# Revit family: Maxlogic  Module  E- S  Adressable Intelligent
name_source: partatom
category: Fire Alarm Devices
units: mm (PartAtom-declared; Revit-internal decimal feet)

## family parameters
Cut with Voids When Loaded = No
Host = Face
Maintain Annotation Orientation = Yes
OmniClass Number = 23.85.30.21
OmniClass Title = Environmental Detection/Registration
Part Type = Normal
Room Calculation Point = No
Round Connector Dimension = Use Diameter
Shared = No

## types (9) — shared parameters
Adresse ligne 1 = Şerifali Mahallesi Kutup Sokak No:27/1-2-4 Ümraniye TR-34775 İSTANBUL
Couleur = Blanc
Deuxime Matèriel = Plastique
Durée de la garantie Travail = 2
Durée de la garantie réservé = 2
Hauteur Nominale = 100 mm
Largeur Nominale = 52 mm
Longeur Nominale = 100 mm
Manuel d'installation = https://mavilielektronik.com
Manufacturer = Mavili Elektronik Ticaret A.Ş.
Matériel Principe = Plastique Blanche PC/ABS
Model = MaxLogic
Numèro de Fax = (+)90 216 466 45 10
Poids = 135 gr
Surface de Montage = Montage à Mur
Tempèrature de Fonctionnement = (-10°C) - (+55°C)
URL = https://www.mavili.com.tr
Unité de durée de garantie = Ans
Voltage de fonctionnement (default) = 26 V/DC
voltage fonction d'opération = 18-33V/DC
zero-valued in all types: Cost, Default Elevation

## per-type parameters (varying)
| type | Charger adresse d'appareil | Code de  Performance | Code de Produit | Description | Numéro de pose des travaux publics |
| Maxlogic Relais Contrôle de Module Adressable, 1 Sortie | Appareil d'adressage à Main | EN 54-18 | ML-1361 | Adresli röle kontrol modülü, 1 çıkış | 833-570 |
| Maxlogic Relais Contrôle de Module Adressable, Isolateur de Court-Circuit | Appareil d'adressage à main | EN 54-18 | ML-1361.SCI | Adresli röle kontrol modülü, Kısa Devre İzolatörlü | 833-571 |
| Maxlogic Module Relais de Surveillance Adressable, 1 Entrée | Appareil d'adressage à Main | EN 54-18 | ML-1362 | Adresli kontak izleme modülü, 1 giriş | 833-575 |
| Module Relais de Surveillance de contact Adressable, 1 Entrée, Isolateur de Court-Circuit | Appareil d'adressage à main | EN 54-18 | ML-1362.SCI | Adresli kontak izleme modülü, Kısa Devre İzolatörlü | 833-576 |
| Maxlogic module 2E/1S Adressable, 2 Surveillance de Contact,1 sortie de relais | Appareil d'adressage à Main | EN 54-18 | ML-1363 | Adresli 2/1 I/O modül, 2 kontak izleme,1 röle çıkışı |  |
| Maxlogic  Module Relais de Surveillance de contact Adressable, 1 Entrée, Isolateur de Court-Circuit | Appareil d'adressage à Main | EN 54-18 | ML-1363.SCI | Adresli 2/1 I/O modül, 2 kontak izleme,1 röle çıkışı, Kısa Devre İzolatörlü |  |
| Maxlogic  module 4E/12S Adressable, 4 Surveillance de Contact,2 sortie de relais, | Appareil d'adressage à Main | EN 54-18 | ML-1366 | Adresli 4/2 I/O modül, 4 kontak izleme,2 röle çıkışı |  |
| Maxlogic module 4E/12S Adressable, 4 Surveillance de Contact,2 sortie de relais, Isolateur de Court-Circuit | Appareil d'adressage à Main | EN 54-18 | ML-1366.SCI | Adresli 4/2 I/O modül, 4 kontak izleme,2 röle çıkışı, Kısa devre izolatörlü |  |
| Maxlogic Module Isolateur de Court-Circuit Système Adressable | Appareil d'adressage à Main | EN 54-17
EN
54-17 | ML-1380 | Adresli Sistem Kısa Devre İzolatör Modülü | 833-580 |

## geometry (parser evidence)
native form markers: Sweep x1
no freeform markers — native parametric forms only
